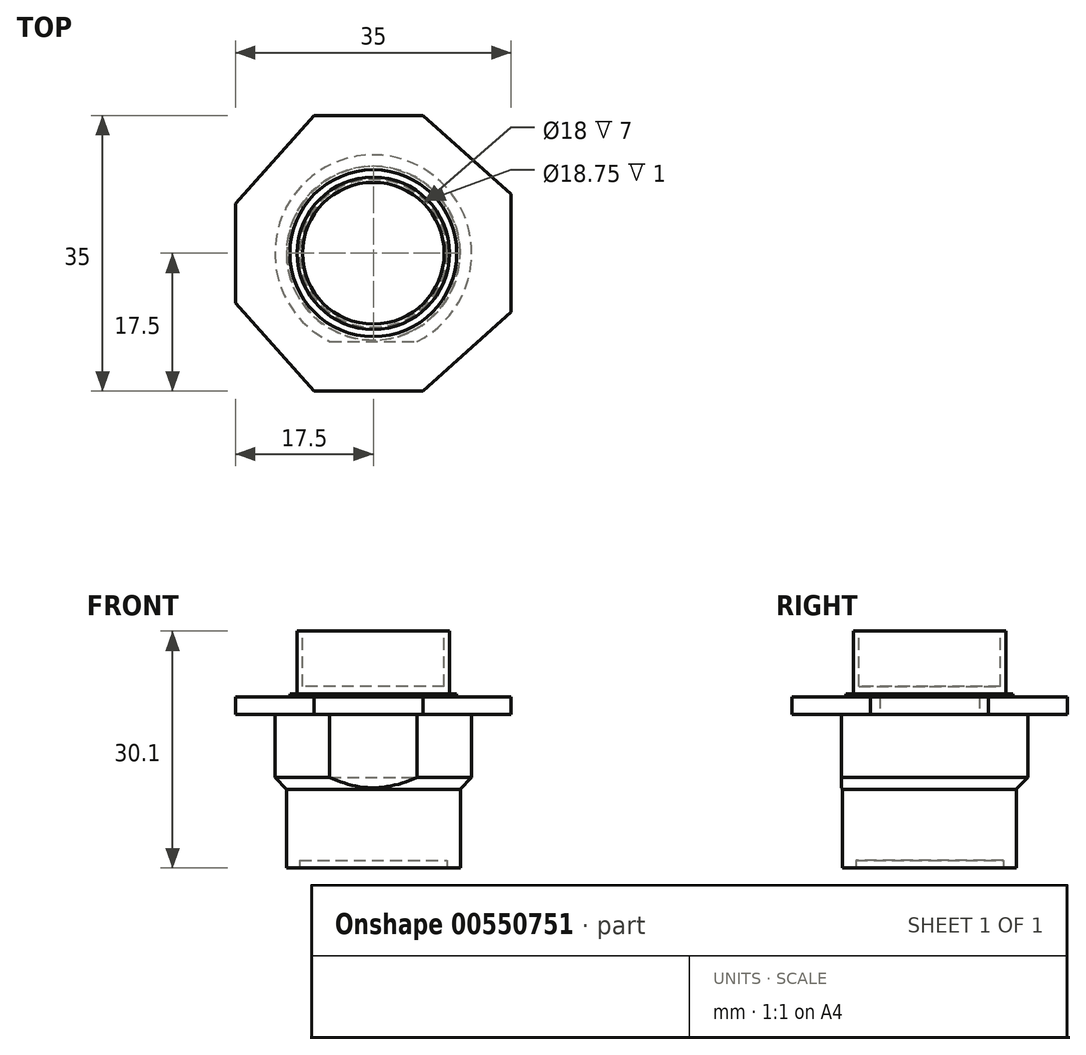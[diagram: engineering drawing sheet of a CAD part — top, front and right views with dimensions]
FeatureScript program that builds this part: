
annotation { "Feature Type Name" : "Feature", "Feature Type Description" : "" }
export const myFeature = defineFeature(function(context is Context, id is Id, definition is map)
    precondition{}
    {
        {
            var Q0;
            Q0=qCreatedBy(makeId("Top.planeOp"),FACE);
            var sketch = newSketch(context, id + "F0", { "sketchPlane" : qUnion([Q0])});
            skLineSegment(sketch, "E0.bottom", {"start": v(0, 0) * mm, "end": v(35, 0) * mm});
            skLineSegment(sketch, "E0.top", {"start": v(0, 35) * mm, "end": v(35, 35) * mm});
            skLineSegment(sketch, "E0.left", {"start": v(0, 0) * mm, "end": v(0, 35) * mm});
            skLineSegment(sketch, "E0.right", {"start": v(35, 0) * mm, "end": v(35, 35) * mm});
            skLineSegment(sketch, "E1", {"start": v(23.82, 35) * mm, "end": v(35, 25) * mm});
            skLineSegment(sketch, "E2", {"start": v(35, 10) * mm, "end": v(23.82, 0) * mm});
            skLineSegment(sketch, "E3", {"start": v(0, 11.18) * mm, "end": v(10, 0) * mm});
            skLineSegment(sketch, "E4", {"start": v(0, 23.82) * mm, "end": v(10, 35) * mm});
            skSolve(sketch);
        }
        {
            var Q0;
            {var subQ0=sQuery(id+"F0.wireOp",EDGE,"E1");Q0=makeQuery(id+"F0.imprint","IMPRINT",FACE,{"disambiguationData":[TD([[makeQuery(id+"F0.imprint","IMPRINT",EDGE,{"derivedFrom":subQ0}),-1.0]])]});}
            extrude(context, id + "F1", {"entities" : qUnion([Q0]), "depth" : 2.25 * mm, "offsetDistance" : 25 * mm});
        }
        {
            var Q0;
            Q0=qCreatedBy(makeId("Top.planeOp"),FACE);
            var sketch = newSketch(context, id + "F2", { "sketchPlane" : qUnion([Q0])});
            skCircle(sketch, "E5", {"center": v(17.5, 17.5) * mm, "radius": 10.6 * mm});
            skSolve(sketch);
        }
        {
            var Q0;
            Q0=makeQuery(id+"F2.imprint","IMPRINT",FACE,{"disambiguationData":[TD([[makeQuery(id+"F2.imprint","IMPRINT",EDGE,{"derivedFrom":sQuery(id+"F2.wireOp",EDGE,"E5")}),1.0]])]});
            extrude(context, id + "F3", {"entities" : qUnion([Q0]), "operationType" : NewBodyOperationType.ADD, "depth" : 10.6 * mm, "offsetDistance" : 25 * mm});
        }
        {
            var Q0;
            Q0=makeQuery(id+"F1.opExtrude","CAP_FACE",FACE,{"disambiguationData":[OSD([sQuery(id+"F0.wireOp",EDGE,"E0.bottom"),sQuery(id+"F0.wireOp",EDGE,"E0.top"),sQuery(id+"F0.wireOp",EDGE,"E0.left"),sQuery(id+"F0.wireOp",EDGE,"E0.right"),sQuery(id+"F0.wireOp",EDGE,"E1"),sQuery(id+"F0.wireOp",EDGE,"E2"),sQuery(id+"F0.wireOp",EDGE,"E3"),sQuery(id+"F0.wireOp",EDGE,"E4")])],"isStart":true});
            var sketch = newSketch(context, id + "F4", { "sketchPlane" : qUnion([Q0])});
            skCircle(sketch, "E6", {"center": v(17.5, -17.5) * mm, "radius": 12.5 * mm});
            skLineSegment(sketch, "E7", {"start": v(11.95, -6.3) * mm, "end": v(23.05, -6.3) * mm});
            skSolve(sketch);
        }
        {
            var Q0;
            {var subQ0=sQuery(id+"F4.wireOp",EDGE,"E7");Q0=makeQuery(id+"F4.imprint","IMPRINT",FACE,{"disambiguationData":[TD([[makeQuery(id+"F4.imprint","IMPRINT",EDGE,{"derivedFrom":subQ0}),-1.0]])]});}
            extrude(context, id + "F5", {"entities" : qUnion([Q0]), "operationType" : NewBodyOperationType.ADD, "depth" : 9.5 * mm, "offsetDistance" : 25 * mm});
        }
        {
            var Q0;
            Q0=makeQuery(id+"F5.opExtrude","CAP_EDGE",EDGE,{"disambiguationData":[OSD([sQuery(id+"F4.wireOp",EDGE,"E6")])],"isStart":false});
            chamfer(context, id + "F6", {"entities" : qUnion([Q0]), "width" : 1.5 * mm, "tangentPropagation" : true});
        }
        {
            var Q0;
            Q0=makeQuery(id+"F5.opExtrude","CAP_FACE",FACE,{"disambiguationData":[OSD([sQuery(id+"F4.wireOp",EDGE,"E6"),sQuery(id+"F4.wireOp",EDGE,"E7")])],"isStart":false});
            var sketch = newSketch(context, id + "F7", { "sketchPlane" : qUnion([Q0])});
            skCircle(sketch, "E8", {"center": v(17.5, -17.5) * mm, "radius": 11.05 * mm});
            skSolve(sketch);
        }
        {
            var Q0;
            Q0 = qSketchRegion(id + "F7", true);
            extrude(context, id + "F8", {"entities" : qUnion([Q0]), "operationType" : NewBodyOperationType.ADD, "depth" : 10 * mm, "offsetDistance" : 25 * mm});
        }
        {
            var Q0;
            Q0=makeQuery(id+"F3.opExtrude","CAP_FACE",FACE,{"disambiguationData":[OSD([sQuery(id+"F2.wireOp",EDGE,"E5")])],"isStart":false});
            var sketch = newSketch(context, id + "F9", { "sketchPlane" : qUnion([Q0])});
            skCircle(sketch, "E9", {"center": v(17.5, 17.5) * mm, "radius": 9 * mm});
            skSolve(sketch);
        }
        {
            var Q0;
            Q0 = qSketchRegion(id + "F9", true);
            extrude(context, id + "F10", {"entities" : qUnion([Q0]), "operationType" : NewBodyOperationType.REMOVE, "oppositeDirection" : true, "depth" : 7 * mm, "offsetDistance" : 25 * mm});
        }
        {
            var Q0;
            Q0=makeQuery(id+"F3.opExtrude","CAP_FACE",FACE,{"disambiguationData":[OSD([sQuery(id+"F2.wireOp",EDGE,"E5")])],"isStart":false});
            var sketch = newSketch(context, id + "F11", { "sketchPlane" : qUnion([Q0])});
            skCircle(sketch, "E10", {"center": v(17.5, 17.5) * mm, "radius": 9.67 * mm});
            skSolve(sketch);
        }
        {
            var Q0;
            Q0=makeQuery(id+"F11.imprint","IMPRINT",FACE,{"disambiguationData":[TD([[makeQuery(id+"F11.imprint","IMPRINT",EDGE,{"derivedFrom":sQuery(id+"F11.wireOp",EDGE,"E10")}),-1.0]])]});
            extrude(context, id + "F12", {"entities" : qUnion([Q0]), "operationType" : NewBodyOperationType.REMOVE, "oppositeDirection" : true, "depth" : 8 * mm, "offsetDistance" : 25 * mm});
        }
        {
            var Q0;
            Q0=makeQuery(id+"F8.opExtrude","CAP_FACE",FACE,{"disambiguationData":[OSD([sQuery(id+"F7.wireOp",EDGE,"E8")])],"isStart":false});
            var sketch = newSketch(context, id + "F13", { "sketchPlane" : qUnion([Q0])});
            skCircle(sketch, "E11", {"center": v(17.5, -17.5) * mm, "radius": 9.38 * mm});
            skSolve(sketch);
        }
        {
            var Q0;
            Q0 = qSketchRegion(id + "F13", true);
            extrude(context, id + "F14", {"entities" : qUnion([Q0]), "operationType" : NewBodyOperationType.REMOVE, "oppositeDirection" : true, "depth" : 1 * mm, "offsetDistance" : 25 * mm});
        }
    });
